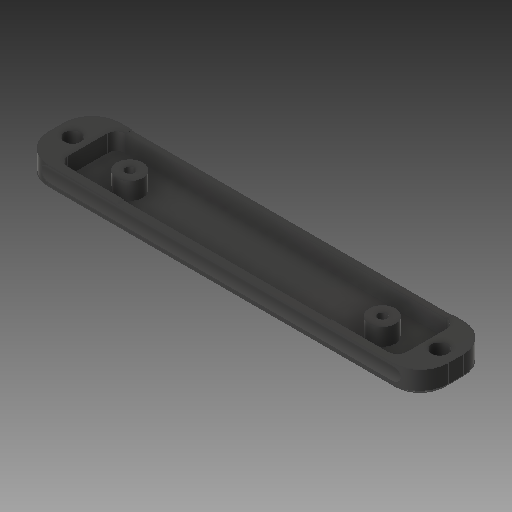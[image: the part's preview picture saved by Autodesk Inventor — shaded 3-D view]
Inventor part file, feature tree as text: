
AUTODESK INVENTOR PART (.ipt)
format: ipt  version: 2019 (Build 230136000, 136)  size: 217,600 bytes
history: native  units: mm
features: other x6, extrude x4, hole x1, fillet x1, chamfer x1
ambient origin geometry x8: Origin, YZ Plane, XZ Plane, XY Plane, X Axis, Y Axis, Z Axis, Center Point
bodies: Solid1 (feature_tree), Body (feature_tree)
feature tree (13):
  extrude  "Body Cutout"  Depth=38.0mm
  extrude  "Skin Passages"  Depth=19.0mm
  hole  "Fastening Holes"  [1 undecoded]
  extrude  "Thumbscrew Holes"  Depth=106.0mm
  extrude  "Side Cutout"  Depth=12.0mm TaperAngle=0.0deg
  fillet  "Body Fillet"  Radius=31.0mm
  chamfer  "Body Chamfer"  Distance=180.0mm
  other  "Body Outline"
  other  "Body Cutout Outline"
  other  "Skin Passages Outline"
  other  "Fastening Hole Positions"
  other  "Thumbscrew Hole Positions"
  other  "Side Cutout Outline"
note: 1 required parameter value undecoded (feature->parameter linkage not recoverable at this tier; creation-order binding heuristic only, values carry confidence <= 0.55)
